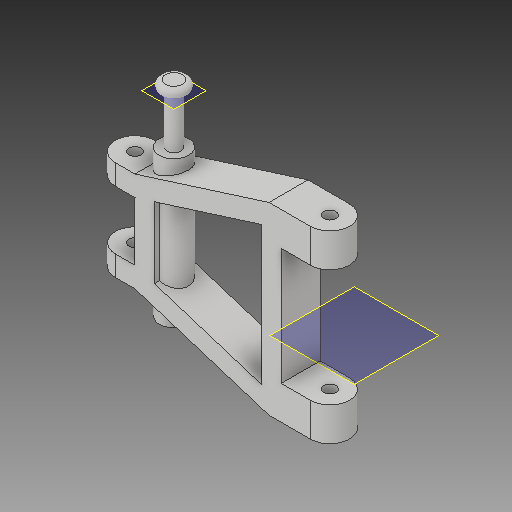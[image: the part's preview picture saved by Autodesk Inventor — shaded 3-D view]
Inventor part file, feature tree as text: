
AUTODESK INVENTOR PART (.ipt)
format: ipt  version: 2019 (Build 230136000, 136)  size: 190,464 bytes
history: native  units: in
note: dims shown in document units (in); Inventor stores cm internally (conversion verified against a paired STEP export)
features: sketch x9, other x3, plane x2
ambient origin geometry x8: Origin, YZ Plane, XZ Plane, XY Plane, X Axis, Y Axis, Z Axis, Center Point
bodies: Solid1 (feature_tree)
feature tree (14):
  other  "A_Arm.ipt"
  other  "Solid1::A_Arm.ipt"
  other  "TaggingFeature1"
  sketch  "Sketch2"  dims[d0=0.3937in]
  sketch  "Sketch3"
  sketch  "Sketch4"
  sketch  "Sketch6"
  sketch  "Sketch5"
  sketch  "Sketch8"
  sketch  "Sketch9"
  sketch  "Sketch10"
  sketch  "Sketch11"
  plane  "Work Plane1"
  plane  "Work Plane2"
